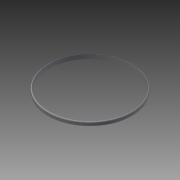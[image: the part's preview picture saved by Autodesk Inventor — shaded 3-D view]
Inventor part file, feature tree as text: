
AUTODESK INVENTOR PART (.ipt)
format: ipt  version: 2015 (Build 190159000, 159)  size: 87,552 bytes
history: native  units: in
note: dims shown in document units (in); Inventor stores cm internally (conversion verified against a paired STEP export)
features: fillet x2, extrude x1, sketch x1
ambient origin geometry x8: Origin, YZ Plane, XZ Plane, XY Plane, X Axis, Y Axis, Z Axis, Center Point
bodies: Solid1 (feature_tree)
feature tree (4):
  extrude  "Extrusion1"  Depth=0.125in
  fillet  "Fillet1"  Radius=0.5in
  fillet  "Fillet2"  Radius=0.125in
  sketch  "Sketch1"  dims[d0=9.8in d1=10.0in d2=0.5in d3=0.0in d4=0.125in d5=0.125in]
